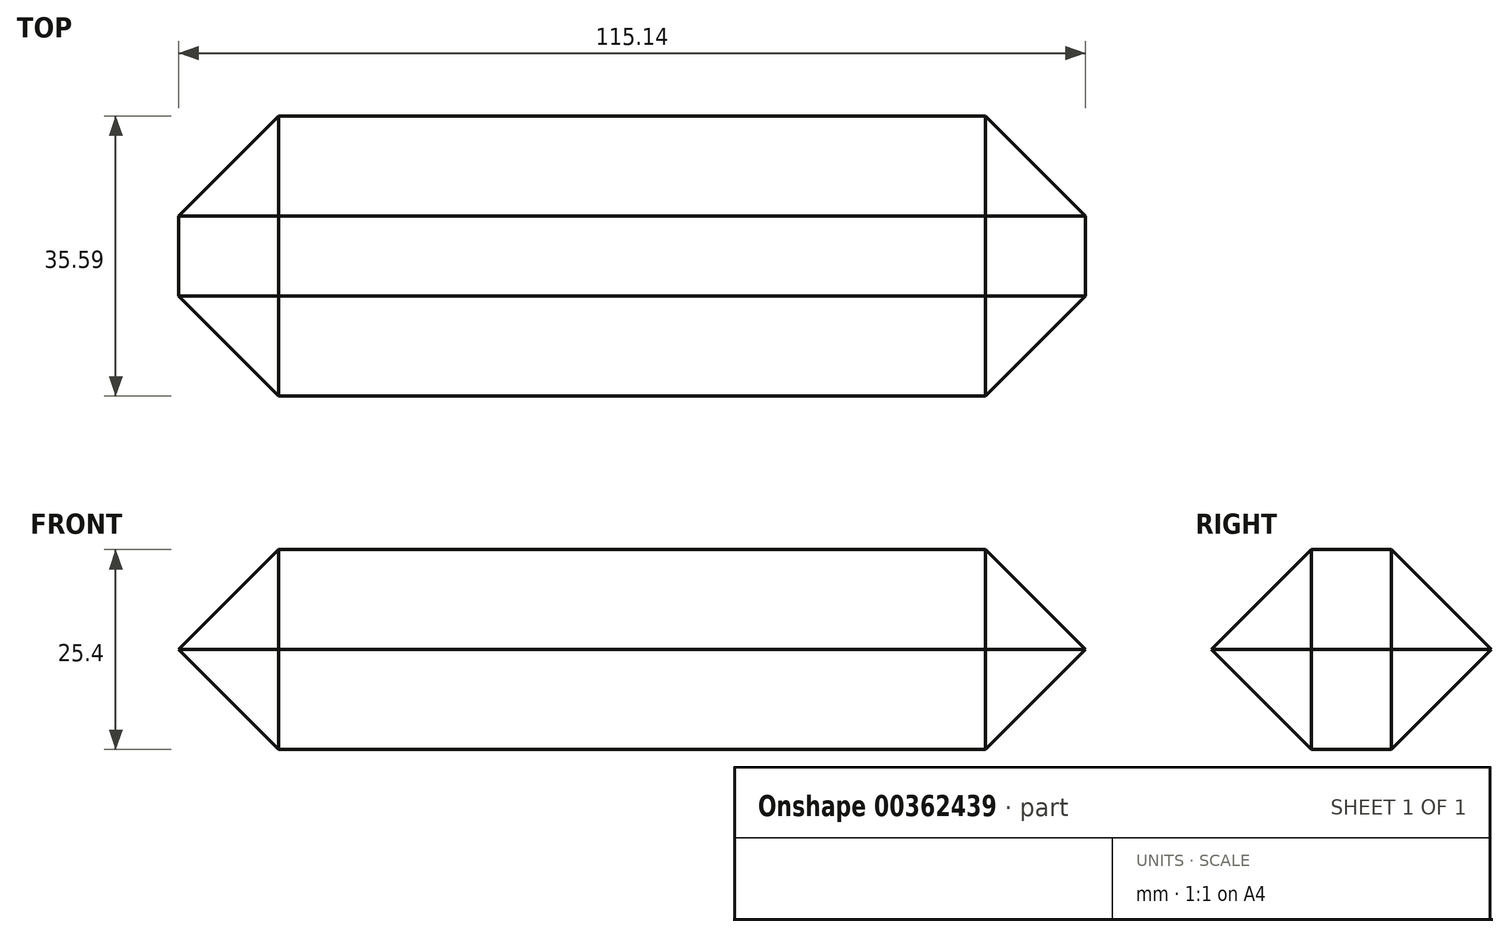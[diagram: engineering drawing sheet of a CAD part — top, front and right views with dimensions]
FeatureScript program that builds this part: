
annotation { "Feature Type Name" : "Feature", "Feature Type Description" : "" }
export const myFeature = defineFeature(function(context is Context, id is Id, definition is map)
    precondition{}
    {
        {
            var Q0;
            Q0=qCreatedBy(makeId("Top.planeOp"),FACE);
            var sketch = newSketch(context, id + "F0", { "sketchPlane" : qUnion([Q0])});
            skLineSegment(sketch, "E0.bottom", {"start": v(-57.57, 21.12) * mm, "end": v(57.57, 21.12) * mm});
            skLineSegment(sketch, "E0.top", {"start": v(-57.57, -14.47) * mm, "end": v(57.57, -14.47) * mm});
            skLineSegment(sketch, "E0.left", {"start": v(-57.57, 21.12) * mm, "end": v(-57.57, -14.47) * mm});
            skLineSegment(sketch, "E0.right", {"start": v(57.57, 21.12) * mm, "end": v(57.57, -14.47) * mm});
            skPoint(sketch, "E0.middle", {"position": v(0, 3.33) * mm});
            skSolve(sketch);
        }
        {
            var Q0;
            Q0 = qSketchRegion(id + "F0", true);
            extrude(context, id + "F1", {"entities" : qUnion([Q0]), "depth" : 25.4 * mm});
        }
        {
            var Q0;
            Q0=makeQuery(id+"F1.opExtrude","CAP_EDGE",EDGE,{"disambiguationData":[OSD([sQuery(id+"F0.wireOp",EDGE,"E0.top")])],"isStart":true});
            var Q1;
            Q1=makeQuery(id+"F1.opExtrude","SWEPT_EDGE",EDGE,{"disambiguationData":[OSD([sQuery(id+"F0.wireOp",EDGE,"E0.bottom"),sQuery(id+"F0.wireOp",EDGE,"E0.right")])]});
            var Q2;
            Q2=makeQuery(id+"F1.opExtrude","SWEPT_EDGE",EDGE,{"disambiguationData":[OSD([sQuery(id+"F0.wireOp",EDGE,"E0.top"),sQuery(id+"F0.wireOp",EDGE,"E0.right")])]});
            var Q3;
            Q3=makeQuery(id+"F1.opExtrude","CAP_EDGE",EDGE,{"disambiguationData":[OSD([sQuery(id+"F0.wireOp",EDGE,"E0.right")])],"isStart":true});
            var Q4;
            Q4=makeQuery(id+"F1.opExtrude","CAP_EDGE",EDGE,{"disambiguationData":[OSD([sQuery(id+"F0.wireOp",EDGE,"E0.right")])],"isStart":false});
            var Q5;
            Q5=makeQuery(id+"F1.opExtrude","CAP_EDGE",EDGE,{"disambiguationData":[OSD([sQuery(id+"F0.wireOp",EDGE,"E0.bottom")])],"isStart":false});
            var Q6;
            Q6=makeQuery(id+"F1.opExtrude","CAP_EDGE",EDGE,{"disambiguationData":[OSD([sQuery(id+"F0.wireOp",EDGE,"E0.bottom")])],"isStart":true});
            var Q7;
            Q7=makeQuery(id+"F1.opExtrude","SWEPT_EDGE",EDGE,{"disambiguationData":[OSD([sQuery(id+"F0.wireOp",EDGE,"E0.bottom"),sQuery(id+"F0.wireOp",EDGE,"E0.left")])]});
            var Q8;
            Q8=makeQuery(id+"F1.opExtrude","CAP_EDGE",EDGE,{"disambiguationData":[OSD([sQuery(id+"F0.wireOp",EDGE,"E0.top")])],"isStart":false});
            var Q9;
            Q9=makeQuery(id+"F1.opExtrude","CAP_EDGE",EDGE,{"disambiguationData":[OSD([sQuery(id+"F0.wireOp",EDGE,"E0.left")])],"isStart":true});
            var Q10;
            Q10=makeQuery(id+"F1.opExtrude","SWEPT_EDGE",EDGE,{"disambiguationData":[OSD([sQuery(id+"F0.wireOp",EDGE,"E0.top"),sQuery(id+"F0.wireOp",EDGE,"E0.left")])]});
            var Q11;
            Q11=makeQuery(id+"F1.opExtrude","CAP_EDGE",EDGE,{"disambiguationData":[OSD([sQuery(id+"F0.wireOp",EDGE,"E0.left")])],"isStart":false});
            chamfer(context, id + "F2", {"entities" : qUnion([Q0, Q1, Q2, Q3, Q4, Q5, Q6, Q7, Q8, Q9, Q10, Q11]), "width" : 12.7 * mm, "tangentPropagation" : true});
        }
    });
